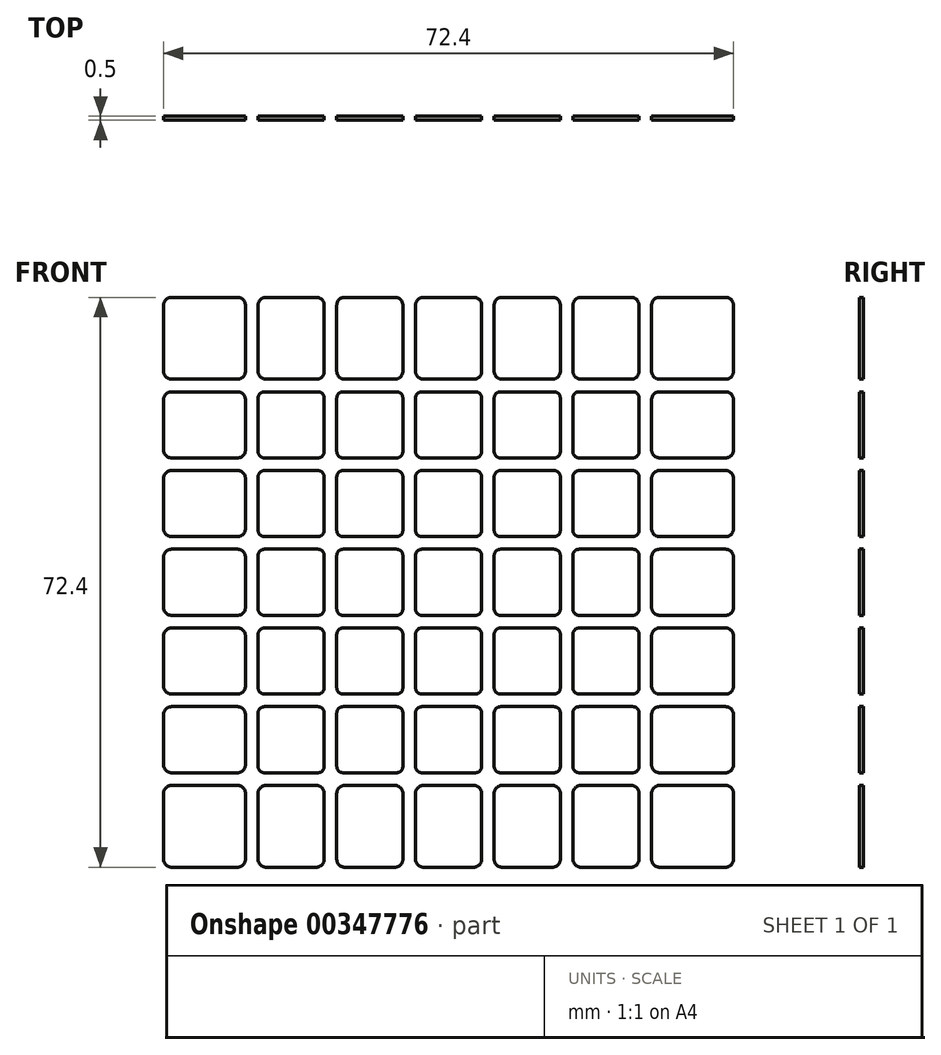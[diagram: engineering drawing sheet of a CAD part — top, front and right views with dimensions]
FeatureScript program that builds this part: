
annotation { "Feature Type Name" : "Feature", "Feature Type Description" : "" }
export const myFeature = defineFeature(function(context is Context, id is Id, definition is map)
    precondition{}
    {
        {
            var Q0;
            Q0=qCreatedBy(makeId("Front.planeOp"),FACE);
            var sketch = newSketch(context, id + "F0", { "sketchPlane" : qUnion([Q0])});
            skLineSegment(sketch, "E0.bottom", {"start": v(3.4, 4.2) * mm, "end": v(-3.4, 4.2) * mm});
            skLineSegment(sketch, "E0.top", {"start": v(3.4, -4.2) * mm, "end": v(-3.4, -4.2) * mm});
            skLineSegment(sketch, "E0.left", {"start": v(4.2, 3.4) * mm, "end": v(4.2, -3.4) * mm});
            skLineSegment(sketch, "E0.right", {"start": v(-4.2, 3.4) * mm, "end": v(-4.2, -3.4) * mm});
            skPoint(sketch, "E0.middle", {"position": v(0, 0) * mm});
            skPoint(sketch, "E1.visualSharp", {"position": v(-4.2, 4.2) * mm});
            skArc(sketch, "E1.filletArc", {"start": v(-3.4, 4.2) * mm, "mid": v(-3.97, 3.97) * mm, "end": v(-4.2, 3.4) * mm});
            skPoint(sketch, "E2.visualSharp", {"position": v(4.2, -4.2) * mm});
            skArc(sketch, "E2.filletArc", {"start": v(3.4, -4.2) * mm, "mid": v(3.97, -3.97) * mm, "end": v(4.2, -3.4) * mm});
            skPoint(sketch, "E3.visualSharp", {"position": v(4.2, 4.2) * mm});
            skArc(sketch, "E3.filletArc", {"start": v(4.2, 3.4) * mm, "mid": v(3.97, 3.97) * mm, "end": v(3.4, 4.2) * mm});
            skPoint(sketch, "E4.visualSharp", {"position": v(-4.2, -4.2) * mm});
            skArc(sketch, "E4.filletArc", {"start": v(-4.2, -3.4) * mm, "mid": v(-3.97, -3.97) * mm, "end": v(-3.4, -4.2) * mm});
            skPoint(sketch, "E5.1.0.0", {"position": v(10, 0) * mm});
            skPoint(sketch, "E5.1.0.1", {"position": v(5.8, 4.2) * mm});
            skPoint(sketch, "E5.1.0.2", {"position": v(14.2, -4.2) * mm});
            skLineSegment(sketch, "E5.1.0.3", {"start": v(5.8, 3.4) * mm, "end": v(5.8, -3.4) * mm});
            skLineSegment(sketch, "E5.1.0.4", {"start": v(14.2, 3.4) * mm, "end": v(14.2, -3.4) * mm});
            skPoint(sketch, "E5.1.0.5", {"position": v(14.2, 4.2) * mm});
            skLineSegment(sketch, "E5.1.0.6", {"start": v(13.4, -4.2) * mm, "end": v(6.6, -4.2) * mm});
            skLineSegment(sketch, "E5.1.0.7", {"start": v(13.4, 4.2) * mm, "end": v(6.6, 4.2) * mm});
            skPoint(sketch, "E5.1.0.8", {"position": v(5.8, -4.2) * mm});
            skArc(sketch, "E5.1.0.9", {"start": v(14.2, 3.4) * mm, "mid": v(13.97, 3.97) * mm, "end": v(13.4, 4.2) * mm});
            skArc(sketch, "E5.1.0.10", {"start": v(13.4, -4.2) * mm, "mid": v(13.97, -3.97) * mm, "end": v(14.2, -3.4) * mm});
            skArc(sketch, "E5.1.0.11", {"start": v(6.6, 4.2) * mm, "mid": v(6.03, 3.97) * mm, "end": v(5.8, 3.4) * mm});
            skArc(sketch, "E5.1.0.12", {"start": v(5.8, -3.4) * mm, "mid": v(6.03, -3.97) * mm, "end": v(6.6, -4.2) * mm});
            skPoint(sketch, "E5.2.0.0", {"position": v(20, 0) * mm});
            skPoint(sketch, "E5.2.0.1", {"position": v(15.8, 4.2) * mm});
            skPoint(sketch, "E5.2.0.2", {"position": v(24.2, -4.2) * mm});
            skLineSegment(sketch, "E5.2.0.3", {"start": v(15.8, 3.4) * mm, "end": v(15.8, -3.4) * mm});
            skLineSegment(sketch, "E5.2.0.4", {"start": v(24.2, 3.4) * mm, "end": v(24.2, -3.4) * mm});
            skPoint(sketch, "E5.2.0.5", {"position": v(24.2, 4.2) * mm});
            skLineSegment(sketch, "E5.2.0.6", {"start": v(23.4, -4.2) * mm, "end": v(16.6, -4.2) * mm});
            skLineSegment(sketch, "E5.2.0.7", {"start": v(23.4, 4.2) * mm, "end": v(16.6, 4.2) * mm});
            skPoint(sketch, "E5.2.0.8", {"position": v(15.8, -4.2) * mm});
            skArc(sketch, "E5.2.0.9", {"start": v(24.2, 3.4) * mm, "mid": v(23.97, 3.97) * mm, "end": v(23.4, 4.2) * mm});
            skArc(sketch, "E5.2.0.10", {"start": v(23.4, -4.2) * mm, "mid": v(23.97, -3.97) * mm, "end": v(24.2, -3.4) * mm});
            skArc(sketch, "E5.2.0.11", {"start": v(16.6, 4.2) * mm, "mid": v(16.03, 3.97) * mm, "end": v(15.8, 3.4) * mm});
            skArc(sketch, "E5.2.0.12", {"start": v(15.8, -3.4) * mm, "mid": v(16.03, -3.97) * mm, "end": v(16.6, -4.2) * mm});
            skLineSegment(sketch, "E5.direction1", {"start": v(-4.2, -4.2) * mm, "end": v(5.8, -4.2) * mm, "construction": true});
            skLineSegment(sketch, "E6.bottom", {"start": v(26.8, -4.2) * mm, "end": v(35.2, -4.2) * mm});
            skLineSegment(sketch, "E6.top", {"start": v(26.8, 4.2) * mm, "end": v(35.2, 4.2) * mm});
            skLineSegment(sketch, "E6.left", {"start": v(25.8, -3.2) * mm, "end": v(25.8, 3.2) * mm});
            skLineSegment(sketch, "E6.right", {"start": v(36.2, -3.2) * mm, "end": v(36.2, 3.2) * mm});
            skPoint(sketch, "E7.visualSharp", {"position": v(25.8, 4.2) * mm});
            skArc(sketch, "E7.filletArc", {"start": v(26.8, 4.2) * mm, "mid": v(26.1, 3.9) * mm, "end": v(25.8, 3.2) * mm});
            skPoint(sketch, "E8.visualSharp", {"position": v(25.8, -4.2) * mm});
            skArc(sketch, "E8.filletArc", {"start": v(25.8, -3.2) * mm, "mid": v(26.1, -3.9) * mm, "end": v(26.8, -4.2) * mm});
            skPoint(sketch, "E9.visualSharp", {"position": v(36.2, 4.2) * mm});
            skArc(sketch, "E9.filletArc", {"start": v(36.2, 3.2) * mm, "mid": v(35.9, 3.9) * mm, "end": v(35.2, 4.2) * mm});
            skPoint(sketch, "E10.visualSharp", {"position": v(36.2, -4.2) * mm});
            skArc(sketch, "E10.filletArc", {"start": v(35.2, -4.2) * mm, "mid": v(35.9, -3.9) * mm, "end": v(36.2, -3.2) * mm});
            skPoint(sketch, "E11.0.1.0", {"position": v(24.2, 14.2) * mm});
            skPoint(sketch, "E11.0.1.1", {"position": v(10, 10) * mm});
            skLineSegment(sketch, "E11.0.1.2", {"start": v(15.8, 13.4) * mm, "end": v(15.8, 6.6) * mm});
            skPoint(sketch, "E11.0.1.3", {"position": v(5.8, 5.8) * mm});
            skPoint(sketch, "E11.0.1.4", {"position": v(25.8, 5.8) * mm});
            skPoint(sketch, "E11.0.1.5", {"position": v(24.2, 5.8) * mm});
            skLineSegment(sketch, "E11.0.1.6", {"start": v(25.8, 6.8) * mm, "end": v(25.8, 13.2) * mm});
            skLineSegment(sketch, "E11.0.1.7", {"start": v(13.4, 14.2) * mm, "end": v(6.6, 14.2) * mm});
            skLineSegment(sketch, "E11.0.1.8", {"start": v(23.4, 14.2) * mm, "end": v(16.6, 14.2) * mm});
            skLineSegment(sketch, "E11.0.1.9", {"start": v(26.8, 14.2) * mm, "end": v(35.2, 14.2) * mm});
            skLineSegment(sketch, "E11.0.1.10", {"start": v(5.8, 13.4) * mm, "end": v(5.8, 6.6) * mm});
            skLineSegment(sketch, "E11.0.1.11", {"start": v(26.8, 5.8) * mm, "end": v(35.2, 5.8) * mm});
            skLineSegment(sketch, "E11.0.1.12", {"start": v(36.2, 6.8) * mm, "end": v(36.2, 13.2) * mm});
            skPoint(sketch, "E11.0.1.13", {"position": v(5.8, 14.2) * mm});
            skPoint(sketch, "E11.0.1.14", {"position": v(25.8, 14.2) * mm});
            skPoint(sketch, "E11.0.1.15", {"position": v(14.2, 5.8) * mm});
            skPoint(sketch, "E11.0.1.16", {"position": v(20, 10) * mm});
            skLineSegment(sketch, "E11.0.1.17", {"start": v(14.2, 13.4) * mm, "end": v(14.2, 6.6) * mm});
            skLineSegment(sketch, "E11.0.1.18", {"start": v(13.4, 5.8) * mm, "end": v(6.6, 5.8) * mm});
            skPoint(sketch, "E11.0.1.19", {"position": v(14.2, 14.2) * mm});
            skPoint(sketch, "E11.0.1.20", {"position": v(15.8, 14.2) * mm});
            skPoint(sketch, "E11.0.1.21", {"position": v(36.2, 14.2) * mm});
            skLineSegment(sketch, "E11.0.1.22", {"start": v(23.4, 5.8) * mm, "end": v(16.6, 5.8) * mm});
            skLineSegment(sketch, "E11.0.1.23", {"start": v(24.2, 13.4) * mm, "end": v(24.2, 6.6) * mm});
            skPoint(sketch, "E11.0.1.24", {"position": v(15.8, 5.8) * mm});
            skPoint(sketch, "E11.0.1.25", {"position": v(36.2, 5.8) * mm});
            skArc(sketch, "E11.0.1.26", {"start": v(35.2, 5.8) * mm, "mid": v(35.9, 6.1) * mm, "end": v(36.2, 6.8) * mm});
            skArc(sketch, "E11.0.1.27", {"start": v(13.4, 5.8) * mm, "mid": v(13.97, 6.03) * mm, "end": v(14.2, 6.6) * mm});
            skArc(sketch, "E11.0.1.28", {"start": v(24.2, 13.4) * mm, "mid": v(23.97, 13.97) * mm, "end": v(23.4, 14.2) * mm});
            skArc(sketch, "E11.0.1.29", {"start": v(15.8, 6.6) * mm, "mid": v(16.03, 6.03) * mm, "end": v(16.6, 5.8) * mm});
            skArc(sketch, "E11.0.1.30", {"start": v(14.2, 13.4) * mm, "mid": v(13.97, 13.97) * mm, "end": v(13.4, 14.2) * mm});
            skArc(sketch, "E11.0.1.31", {"start": v(36.2, 13.2) * mm, "mid": v(35.9, 13.9) * mm, "end": v(35.2, 14.2) * mm});
            skArc(sketch, "E11.0.1.32", {"start": v(23.4, 5.8) * mm, "mid": v(23.97, 6.03) * mm, "end": v(24.2, 6.6) * mm});
            skArc(sketch, "E11.0.1.33", {"start": v(6.6, 14.2) * mm, "mid": v(6.03, 13.97) * mm, "end": v(5.8, 13.4) * mm});
            skArc(sketch, "E11.0.1.34", {"start": v(25.8, 6.8) * mm, "mid": v(26.1, 6.1) * mm, "end": v(26.8, 5.8) * mm});
            skArc(sketch, "E11.0.1.35", {"start": v(16.6, 14.2) * mm, "mid": v(16.03, 13.97) * mm, "end": v(15.8, 13.4) * mm});
            skArc(sketch, "E11.0.1.36", {"start": v(26.8, 14.2) * mm, "mid": v(26.1, 13.9) * mm, "end": v(25.8, 13.2) * mm});
            skArc(sketch, "E11.0.1.37", {"start": v(5.8, 6.6) * mm, "mid": v(6.03, 6.03) * mm, "end": v(6.6, 5.8) * mm});
            skPoint(sketch, "E11.0.2.0", {"position": v(24.2, 24.2) * mm});
            skPoint(sketch, "E11.0.2.1", {"position": v(10, 20) * mm});
            skLineSegment(sketch, "E11.0.2.2", {"start": v(15.8, 23.4) * mm, "end": v(15.8, 16.6) * mm});
            skPoint(sketch, "E11.0.2.3", {"position": v(5.8, 15.8) * mm});
            skPoint(sketch, "E11.0.2.4", {"position": v(25.8, 15.8) * mm});
            skPoint(sketch, "E11.0.2.5", {"position": v(24.2, 15.8) * mm});
            skLineSegment(sketch, "E11.0.2.6", {"start": v(25.8, 16.8) * mm, "end": v(25.8, 23.2) * mm});
            skLineSegment(sketch, "E11.0.2.7", {"start": v(13.4, 24.2) * mm, "end": v(6.6, 24.2) * mm});
            skLineSegment(sketch, "E11.0.2.8", {"start": v(23.4, 24.2) * mm, "end": v(16.6, 24.2) * mm});
            skLineSegment(sketch, "E11.0.2.9", {"start": v(26.8, 24.2) * mm, "end": v(35.2, 24.2) * mm});
            skLineSegment(sketch, "E11.0.2.10", {"start": v(5.8, 23.4) * mm, "end": v(5.8, 16.6) * mm});
            skLineSegment(sketch, "E11.0.2.11", {"start": v(26.8, 15.8) * mm, "end": v(35.2, 15.8) * mm});
            skLineSegment(sketch, "E11.0.2.12", {"start": v(36.2, 16.8) * mm, "end": v(36.2, 23.2) * mm});
            skPoint(sketch, "E11.0.2.13", {"position": v(5.8, 24.2) * mm});
            skPoint(sketch, "E11.0.2.14", {"position": v(25.8, 24.2) * mm});
            skPoint(sketch, "E11.0.2.15", {"position": v(14.2, 15.8) * mm});
            skPoint(sketch, "E11.0.2.16", {"position": v(20, 20) * mm});
            skLineSegment(sketch, "E11.0.2.17", {"start": v(14.2, 23.4) * mm, "end": v(14.2, 16.6) * mm});
            skLineSegment(sketch, "E11.0.2.18", {"start": v(13.4, 15.8) * mm, "end": v(6.6, 15.8) * mm});
            skPoint(sketch, "E11.0.2.19", {"position": v(14.2, 24.2) * mm});
            skPoint(sketch, "E11.0.2.20", {"position": v(15.8, 24.2) * mm});
            skPoint(sketch, "E11.0.2.21", {"position": v(36.2, 24.2) * mm});
            skLineSegment(sketch, "E11.0.2.22", {"start": v(23.4, 15.8) * mm, "end": v(16.6, 15.8) * mm});
            skLineSegment(sketch, "E11.0.2.23", {"start": v(24.2, 23.4) * mm, "end": v(24.2, 16.6) * mm});
            skPoint(sketch, "E11.0.2.24", {"position": v(15.8, 15.8) * mm});
            skPoint(sketch, "E11.0.2.25", {"position": v(36.2, 15.8) * mm});
            skArc(sketch, "E11.0.2.26", {"start": v(35.2, 15.8) * mm, "mid": v(35.9, 16.1) * mm, "end": v(36.2, 16.8) * mm});
            skArc(sketch, "E11.0.2.27", {"start": v(13.4, 15.8) * mm, "mid": v(13.97, 16.03) * mm, "end": v(14.2, 16.6) * mm});
            skArc(sketch, "E11.0.2.28", {"start": v(24.2, 23.4) * mm, "mid": v(23.97, 23.97) * mm, "end": v(23.4, 24.2) * mm});
            skArc(sketch, "E11.0.2.29", {"start": v(15.8, 16.6) * mm, "mid": v(16.03, 16.03) * mm, "end": v(16.6, 15.8) * mm});
            skArc(sketch, "E11.0.2.30", {"start": v(14.2, 23.4) * mm, "mid": v(13.97, 23.97) * mm, "end": v(13.4, 24.2) * mm});
            skArc(sketch, "E11.0.2.31", {"start": v(36.2, 23.2) * mm, "mid": v(35.9, 23.9) * mm, "end": v(35.2, 24.2) * mm});
            skArc(sketch, "E11.0.2.32", {"start": v(23.4, 15.8) * mm, "mid": v(23.97, 16.03) * mm, "end": v(24.2, 16.6) * mm});
            skArc(sketch, "E11.0.2.33", {"start": v(6.6, 24.2) * mm, "mid": v(6.03, 23.97) * mm, "end": v(5.8, 23.4) * mm});
            skArc(sketch, "E11.0.2.34", {"start": v(25.8, 16.8) * mm, "mid": v(26.1, 16.1) * mm, "end": v(26.8, 15.8) * mm});
            skArc(sketch, "E11.0.2.35", {"start": v(16.6, 24.2) * mm, "mid": v(16.03, 23.97) * mm, "end": v(15.8, 23.4) * mm});
            skArc(sketch, "E11.0.2.36", {"start": v(26.8, 24.2) * mm, "mid": v(26.1, 23.9) * mm, "end": v(25.8, 23.2) * mm});
            skArc(sketch, "E11.0.2.37", {"start": v(5.8, 16.6) * mm, "mid": v(6.03, 16.03) * mm, "end": v(6.6, 15.8) * mm});
            skLineSegment(sketch, "E11.direction1", {"start": v(5.8, -4.2) * mm, "end": v(32.07, -4.2) * mm, "construction": true});
            skLineSegment(sketch, "E11.direction2", {"start": v(5.8, -4.2) * mm, "end": v(5.8, 5.8) * mm, "construction": true});
            skLineSegment(sketch, "E12.bottom", {"start": v(26.8, 25.8) * mm, "end": v(35.2, 25.8) * mm});
            skLineSegment(sketch, "E12.top", {"start": v(26.8, 36.2) * mm, "end": v(35.2, 36.2) * mm});
            skLineSegment(sketch, "E12.left", {"start": v(25.8, 26.8) * mm, "end": v(25.8, 35.2) * mm});
            skLineSegment(sketch, "E12.right", {"start": v(36.2, 26.8) * mm, "end": v(36.2, 35.2) * mm});
            skPoint(sketch, "E13.visualSharp", {"position": v(25.8, 25.8) * mm});
            skArc(sketch, "E13.filletArc", {"start": v(25.8, 26.8) * mm, "mid": v(26.1, 26.1) * mm, "end": v(26.8, 25.8) * mm});
            skPoint(sketch, "E14.visualSharp", {"position": v(36.2, 25.8) * mm});
            skArc(sketch, "E14.filletArc", {"start": v(35.2, 25.8) * mm, "mid": v(35.9, 26.1) * mm, "end": v(36.2, 26.8) * mm});
            skPoint(sketch, "E15.visualSharp", {"position": v(36.2, 36.2) * mm});
            skArc(sketch, "E15.filletArc", {"start": v(36.2, 35.2) * mm, "mid": v(35.9, 35.9) * mm, "end": v(35.2, 36.2) * mm});
            skPoint(sketch, "E16.visualSharp", {"position": v(25.8, 36.2) * mm});
            skArc(sketch, "E16.filletArc", {"start": v(26.8, 36.2) * mm, "mid": v(26.1, 35.9) * mm, "end": v(25.8, 35.2) * mm});
            skPoint(sketch, "E17.0.1.0", {"position": v(36.2, -5.8) * mm});
            skPoint(sketch, "E17.0.1.1", {"position": v(36.2, -14.2) * mm});
            skLineSegment(sketch, "E17.0.1.2", {"start": v(36.2, -13.2) * mm, "end": v(36.2, -6.8) * mm});
            skLineSegment(sketch, "E17.0.1.3", {"start": v(25.8, -13.2) * mm, "end": v(25.8, -6.8) * mm});
            skPoint(sketch, "E17.0.1.4", {"position": v(25.8, -5.8) * mm});
            skLineSegment(sketch, "E17.0.1.5", {"start": v(26.8, -14.2) * mm, "end": v(35.2, -14.2) * mm});
            skLineSegment(sketch, "E17.0.1.6", {"start": v(26.8, -5.8) * mm, "end": v(35.2, -5.8) * mm});
            skPoint(sketch, "E17.0.1.7", {"position": v(25.8, -14.2) * mm});
            skArc(sketch, "E17.0.1.8", {"start": v(26.8, -5.8) * mm, "mid": v(26.1, -6.1) * mm, "end": v(25.8, -6.8) * mm});
            skArc(sketch, "E17.0.1.9", {"start": v(25.8, -13.2) * mm, "mid": v(26.1, -13.9) * mm, "end": v(26.8, -14.2) * mm});
            skArc(sketch, "E17.0.1.10", {"start": v(36.2, -6.8) * mm, "mid": v(35.9, -6.1) * mm, "end": v(35.2, -5.8) * mm});
            skArc(sketch, "E17.0.1.11", {"start": v(35.2, -14.2) * mm, "mid": v(35.9, -13.9) * mm, "end": v(36.2, -13.2) * mm});
            skPoint(sketch, "E17.0.2.0", {"position": v(36.2, -15.8) * mm});
            skPoint(sketch, "E17.0.2.1", {"position": v(36.2, -24.2) * mm});
            skLineSegment(sketch, "E17.0.2.2", {"start": v(36.2, -23.2) * mm, "end": v(36.2, -16.8) * mm});
            skLineSegment(sketch, "E17.0.2.3", {"start": v(25.8, -23.2) * mm, "end": v(25.8, -16.8) * mm});
            skPoint(sketch, "E17.0.2.4", {"position": v(25.8, -15.8) * mm});
            skLineSegment(sketch, "E17.0.2.5", {"start": v(26.8, -24.2) * mm, "end": v(35.2, -24.2) * mm});
            skLineSegment(sketch, "E17.0.2.6", {"start": v(26.8, -15.8) * mm, "end": v(35.2, -15.8) * mm});
            skPoint(sketch, "E17.0.2.7", {"position": v(25.8, -24.2) * mm});
            skArc(sketch, "E17.0.2.8", {"start": v(26.8, -15.8) * mm, "mid": v(26.1, -16.1) * mm, "end": v(25.8, -16.8) * mm});
            skArc(sketch, "E17.0.2.9", {"start": v(25.8, -23.2) * mm, "mid": v(26.1, -23.9) * mm, "end": v(26.8, -24.2) * mm});
            skArc(sketch, "E17.0.2.10", {"start": v(36.2, -16.8) * mm, "mid": v(35.9, -16.1) * mm, "end": v(35.2, -15.8) * mm});
            skArc(sketch, "E17.0.2.11", {"start": v(35.2, -24.2) * mm, "mid": v(35.9, -23.9) * mm, "end": v(36.2, -23.2) * mm});
            skLineSegment(sketch, "E17.direction1", {"start": v(25.8, -4.2) * mm, "end": v(50.07, -4.2) * mm, "construction": true});
            skLineSegment(sketch, "E17.direction2", {"start": v(25.8, -4.2) * mm, "end": v(25.8, -14.2) * mm, "construction": true});
            skLineSegment(sketch, "E18.1.0", {"start": v(-4.2, 26.8) * mm, "end": v(-4.2, 35.2) * mm});
            skPoint(sketch, "E18.1.1", {"position": v(14.2, 36.2) * mm});
            skLineSegment(sketch, "E18.1.2", {"start": v(-16.8, 25.8) * mm, "end": v(-23.2, 25.8) * mm});
            skPoint(sketch, "E18.1.3", {"position": v(-20, 20) * mm});
            skPoint(sketch, "E18.1.4", {"position": v(-36.2, 36.2) * mm});
            skLineSegment(sketch, "E18.1.5", {"start": v(4.2, 25.8) * mm, "end": v(14.2, 25.8) * mm, "construction": true});
            skLineSegment(sketch, "E18.1.6", {"start": v(-26.8, 25.8) * mm, "end": v(-35.2, 25.8) * mm});
            skPoint(sketch, "E18.1.7", {"position": v(-15.8, 25.8) * mm});
            skPoint(sketch, "E18.1.8", {"position": v(-4.2, 24.2) * mm});
            skLineSegment(sketch, "E18.1.9", {"start": v(-6.8, 36.2) * mm, "end": v(-13.2, 36.2) * mm});
            skLineSegment(sketch, "E18.1.10", {"start": v(3.2, 36.2) * mm, "end": v(-3.2, 36.2) * mm});
            skPoint(sketch, "E18.1.11", {"position": v(-14.2, 24.2) * mm});
            skLineSegment(sketch, "E18.1.12", {"start": v(24.2, 26.8) * mm, "end": v(24.2, 35.2) * mm});
            skLineSegment(sketch, "E18.1.13", {"start": v(-14.2, 26.8) * mm, "end": v(-14.2, 35.2) * mm});
            skLineSegment(sketch, "E18.1.14", {"start": v(-23.4, 5.8) * mm, "end": v(-16.6, 5.8) * mm});
            skPoint(sketch, "E18.1.15", {"position": v(4.2, 14.2) * mm});
            skPoint(sketch, "E18.1.16", {"position": v(-4.2, 25.8) * mm});
            skPoint(sketch, "E18.1.17", {"position": v(-4.2, 15.8) * mm});
            skPoint(sketch, "E18.1.18", {"position": v(-4.2, 14.2) * mm});
            skPoint(sketch, "E18.1.19", {"position": v(-14.2, 14.2) * mm});
            skLineSegment(sketch, "E18.1.20", {"start": v(-26.8, 36.2) * mm, "end": v(-35.2, 36.2) * mm});
            skLineSegment(sketch, "E18.1.21", {"start": v(-13.4, 5.8) * mm, "end": v(-6.6, 5.8) * mm});
            skLineSegment(sketch, "E18.1.22", {"start": v(15.8, 26.8) * mm, "end": v(15.8, 35.2) * mm});
            skPoint(sketch, "E18.1.23", {"position": v(4.2, 5.8) * mm});
            skLineSegment(sketch, "E18.1.24", {"start": v(5.8, 26.8) * mm, "end": v(5.8, 35.2) * mm});
            skPoint(sketch, "E18.1.25", {"position": v(0, 20) * mm});
            skPoint(sketch, "E18.1.26", {"position": v(-24.2, 24.2) * mm});
            skPoint(sketch, "E18.1.27", {"position": v(-15.8, 5.8) * mm});
            skLineSegment(sketch, "E18.1.28", {"start": v(-15.8, 26.8) * mm, "end": v(-15.8, 35.2) * mm});
            skPoint(sketch, "E18.1.29", {"position": v(-14.2, 15.8) * mm});
            skPoint(sketch, "E18.1.30", {"position": v(-5.8, 15.8) * mm});
            skPoint(sketch, "E18.1.31", {"position": v(-4.2, 36.2) * mm});
            skPoint(sketch, "E18.1.32", {"position": v(4.2, 25.8) * mm});
            skLineSegment(sketch, "E18.1.33", {"start": v(-23.4, 15.8) * mm, "end": v(-16.6, 15.8) * mm});
            skPoint(sketch, "E18.1.34", {"position": v(-24.2, 5.8) * mm});
            skLineSegment(sketch, "E18.1.35", {"start": v(-13.4, 14.2) * mm, "end": v(-6.6, 14.2) * mm});
            skPoint(sketch, "E18.1.36", {"position": v(-36.2, 25.8) * mm});
            skPoint(sketch, "E18.1.37", {"position": v(-5.8, 5.8) * mm});
            skPoint(sketch, "E18.1.38", {"position": v(14.2, 25.8) * mm});
            skLineSegment(sketch, "E18.1.39", {"start": v(-5.8, 26.8) * mm, "end": v(-5.8, 35.2) * mm});
            skLineSegment(sketch, "E18.1.40", {"start": v(-5.8, 13.4) * mm, "end": v(-5.8, 6.6) * mm});
            skLineSegment(sketch, "E18.1.41", {"start": v(-3.4, 14.2) * mm, "end": v(3.4, 14.2) * mm});
            skPoint(sketch, "E18.1.42", {"position": v(5.8, 36.2) * mm});
            skPoint(sketch, "E18.1.43", {"position": v(-5.8, 36.2) * mm});
            skLineSegment(sketch, "E18.1.44", {"start": v(23.2, 25.8) * mm, "end": v(16.8, 25.8) * mm});
            skLineSegment(sketch, "E18.1.45", {"start": v(-14.2, 23.4) * mm, "end": v(-14.2, 16.6) * mm});
            skLineSegment(sketch, "E18.1.46", {"start": v(-23.4, 24.2) * mm, "end": v(-16.6, 24.2) * mm});
            skPoint(sketch, "E18.1.47", {"position": v(-10, 20) * mm});
            skPoint(sketch, "E18.1.48", {"position": v(-20, 10) * mm});
            skPoint(sketch, "E18.1.49", {"position": v(-14.2, 36.2) * mm});
            skLineSegment(sketch, "E18.1.50", {"start": v(-13.4, 24.2) * mm, "end": v(-6.6, 24.2) * mm});
            skLineSegment(sketch, "E18.1.51", {"start": v(-24.2, 23.4) * mm, "end": v(-24.2, 16.6) * mm});
            skPoint(sketch, "E18.1.52", {"position": v(-15.8, 14.2) * mm});
            skLineSegment(sketch, "E18.1.53", {"start": v(-36.2, 26.8) * mm, "end": v(-36.2, 35.2) * mm});
            skPoint(sketch, "E18.1.54", {"position": v(-15.8, 36.2) * mm});
            skPoint(sketch, "E18.1.55", {"position": v(24.2, 25.8) * mm});
            skPoint(sketch, "E18.1.56", {"position": v(-4.2, 5.8) * mm});
            skPoint(sketch, "E18.1.57", {"position": v(-5.8, 14.2) * mm});
            skPoint(sketch, "E18.1.58", {"position": v(4.2, 24.2) * mm});
            skPoint(sketch, "E18.1.59", {"position": v(-10, 10) * mm});
            skLineSegment(sketch, "E18.1.60", {"start": v(23.2, 36.2) * mm, "end": v(16.8, 36.2) * mm});
            skLineSegment(sketch, "E18.1.61", {"start": v(-14.2, 13.4) * mm, "end": v(-14.2, 6.6) * mm});
            skPoint(sketch, "E18.1.62", {"position": v(5.8, 25.8) * mm});
            skLineSegment(sketch, "E18.1.63", {"start": v(-15.8, 23.4) * mm, "end": v(-15.8, 16.6) * mm});
            skPoint(sketch, "E18.1.64", {"position": v(4.2, 36.2) * mm});
            skPoint(sketch, "E18.1.65", {"position": v(-15.8, 24.2) * mm});
            skLineSegment(sketch, "E18.1.66", {"start": v(-25.8, 26.8) * mm, "end": v(-25.8, 35.2) * mm});
            skLineSegment(sketch, "E18.1.67", {"start": v(-4.2, 23.4) * mm, "end": v(-4.2, 16.6) * mm});
            skPoint(sketch, "E18.1.68", {"position": v(-15.8, 15.8) * mm});
            skPoint(sketch, "E18.1.69", {"position": v(-25.8, 36.2) * mm});
            skPoint(sketch, "E18.1.70", {"position": v(15.8, 25.8) * mm});
            skPoint(sketch, "E18.1.71", {"position": v(0, 10) * mm});
            skPoint(sketch, "E18.1.72", {"position": v(-14.2, 25.8) * mm});
            skLineSegment(sketch, "E18.1.73", {"start": v(14.2, 26.8) * mm, "end": v(14.2, 35.2) * mm});
            skPoint(sketch, "E18.1.74", {"position": v(-24.2, 25.8) * mm});
            skLineSegment(sketch, "E18.1.75", {"start": v(-24.2, 13.4) * mm, "end": v(-24.2, 6.6) * mm});
            skLineSegment(sketch, "E18.1.76", {"start": v(-5.8, 23.4) * mm, "end": v(-5.8, 16.6) * mm});
            skLineSegment(sketch, "E18.1.77", {"start": v(3.2, 25.8) * mm, "end": v(-3.2, 25.8) * mm});
            skLineSegment(sketch, "E18.1.78", {"start": v(-4.2, 13.4) * mm, "end": v(-4.2, 6.6) * mm});
            skLineSegment(sketch, "E18.1.79", {"start": v(-24.2, 26.8) * mm, "end": v(-24.2, 35.2) * mm});
            skLineSegment(sketch, "E18.1.80", {"start": v(13.2, 36.2) * mm, "end": v(6.8, 36.2) * mm});
            skPoint(sketch, "E18.1.81", {"position": v(-5.8, 25.8) * mm});
            skPoint(sketch, "E18.1.82", {"position": v(4.2, 15.8) * mm});
            skPoint(sketch, "E18.1.83", {"position": v(-24.2, 14.2) * mm});
            skLineSegment(sketch, "E18.1.84", {"start": v(-3.4, 15.8) * mm, "end": v(3.4, 15.8) * mm});
            skLineSegment(sketch, "E18.1.85", {"start": v(-16.8, 36.2) * mm, "end": v(-23.2, 36.2) * mm});
            skPoint(sketch, "E18.1.86", {"position": v(-5.8, 24.2) * mm});
            skPoint(sketch, "E18.1.87", {"position": v(15.8, 36.2) * mm});
            skPoint(sketch, "E18.1.88", {"position": v(-25.8, 25.8) * mm});
            skPoint(sketch, "E18.1.89", {"position": v(-24.2, 15.8) * mm});
            skLineSegment(sketch, "E18.1.90", {"start": v(-3.4, 24.2) * mm, "end": v(3.4, 24.2) * mm});
            skLineSegment(sketch, "E18.1.91", {"start": v(-23.4, 14.2) * mm, "end": v(-16.6, 14.2) * mm});
            skLineSegment(sketch, "E18.1.92", {"start": v(-13.4, 15.8) * mm, "end": v(-6.6, 15.8) * mm});
            skPoint(sketch, "E18.1.93", {"position": v(-14.2, 5.8) * mm});
            skPoint(sketch, "E18.1.94", {"position": v(24.2, 36.2) * mm});
            skPoint(sketch, "E18.1.95", {"position": v(-24.2, 36.2) * mm});
            skLineSegment(sketch, "E18.1.96", {"start": v(4.2, 5.8) * mm, "end": v(-5.8, 5.8) * mm, "construction": true});
            skLineSegment(sketch, "E18.1.97", {"start": v(-15.8, 13.4) * mm, "end": v(-15.8, 6.6) * mm});
            skLineSegment(sketch, "E18.1.98", {"start": v(-6.8, 25.8) * mm, "end": v(-13.2, 25.8) * mm});
            skLineSegment(sketch, "E18.1.99", {"start": v(-3.4, 5.8) * mm, "end": v(3.4, 5.8) * mm});
            skLineSegment(sketch, "E18.1.100", {"start": v(13.2, 25.8) * mm, "end": v(6.8, 25.8) * mm});
            skLineSegment(sketch, "E18.1.101", {"start": v(4.2, 26.8) * mm, "end": v(4.2, 35.2) * mm});
            skLineSegment(sketch, "E18.1.102", {"start": v(4.2, 13.4) * mm, "end": v(4.2, 6.6) * mm});
            skLineSegment(sketch, "E18.1.103", {"start": v(4.2, 23.4) * mm, "end": v(4.2, 16.6) * mm});
            skArc(sketch, "E18.1.104", {"start": v(-36.2, 26.8) * mm, "mid": v(-35.9, 26.1) * mm, "end": v(-35.2, 25.8) * mm});
            skArc(sketch, "E18.1.105", {"start": v(24.2, 35.2) * mm, "mid": v(23.9, 35.9) * mm, "end": v(23.2, 36.2) * mm});
            skArc(sketch, "E18.1.106", {"start": v(-23.2, 36.2) * mm, "mid": v(-23.9, 35.9) * mm, "end": v(-24.2, 35.2) * mm});
            skArc(sketch, "E18.1.107", {"start": v(4.2, 23.4) * mm, "mid": v(3.97, 23.97) * mm, "end": v(3.4, 24.2) * mm});
            skArc(sketch, "E18.1.108", {"start": v(-5.8, 13.4) * mm, "mid": v(-6.03, 13.97) * mm, "end": v(-6.6, 14.2) * mm});
            skArc(sketch, "E18.1.109", {"start": v(-23.4, 14.2) * mm, "mid": v(-23.97, 13.97) * mm, "end": v(-24.2, 13.4) * mm});
            skArc(sketch, "E18.1.110", {"start": v(-6.6, 5.8) * mm, "mid": v(-6.03, 6.03) * mm, "end": v(-5.8, 6.6) * mm});
            skArc(sketch, "E18.1.111", {"start": v(-15.8, 35.2) * mm, "mid": v(-16.1, 35.9) * mm, "end": v(-16.8, 36.2) * mm});
            skArc(sketch, "E18.1.112", {"start": v(-6.8, 25.8) * mm, "mid": v(-6.1, 26.1) * mm, "end": v(-5.8, 26.8) * mm});
            skArc(sketch, "E18.1.113", {"start": v(-24.2, 16.6) * mm, "mid": v(-23.97, 16.03) * mm, "end": v(-23.4, 15.8) * mm});
            skArc(sketch, "E18.1.114", {"start": v(-24.2, 26.8) * mm, "mid": v(-23.9, 26.1) * mm, "end": v(-23.2, 25.8) * mm});
            skArc(sketch, "E18.1.115", {"start": v(-4.2, 16.6) * mm, "mid": v(-3.97, 16.03) * mm, "end": v(-3.4, 15.8) * mm});
            skArc(sketch, "E18.1.116", {"start": v(-15.8, 13.4) * mm, "mid": v(-16.03, 13.97) * mm, "end": v(-16.6, 14.2) * mm});
            skArc(sketch, "E18.1.117", {"start": v(-14.2, 16.6) * mm, "mid": v(-13.97, 16.03) * mm, "end": v(-13.4, 15.8) * mm});
            skArc(sketch, "E18.1.118", {"start": v(5.8, 26.8) * mm, "mid": v(6.1, 26.1) * mm, "end": v(6.8, 25.8) * mm});
            skArc(sketch, "E18.1.119", {"start": v(4.2, 13.4) * mm, "mid": v(3.97, 13.97) * mm, "end": v(3.4, 14.2) * mm});
            skArc(sketch, "E18.1.120", {"start": v(-25.8, 35.2) * mm, "mid": v(-26.1, 35.9) * mm, "end": v(-26.8, 36.2) * mm});
            skArc(sketch, "E18.1.121", {"start": v(-16.6, 15.8) * mm, "mid": v(-16.03, 16.03) * mm, "end": v(-15.8, 16.6) * mm});
            skArc(sketch, "E18.1.122", {"start": v(-14.2, 26.8) * mm, "mid": v(-13.9, 26.1) * mm, "end": v(-13.2, 25.8) * mm});
            skArc(sketch, "E18.1.123", {"start": v(3.4, 15.8) * mm, "mid": v(3.97, 16.03) * mm, "end": v(4.2, 16.6) * mm});
            skArc(sketch, "E18.1.124", {"start": v(23.2, 25.8) * mm, "mid": v(23.9, 26.1) * mm, "end": v(24.2, 26.8) * mm});
            skArc(sketch, "E18.1.125", {"start": v(15.8, 26.8) * mm, "mid": v(16.1, 26.1) * mm, "end": v(16.8, 25.8) * mm});
            skArc(sketch, "E18.1.126", {"start": v(-26.8, 25.8) * mm, "mid": v(-26.1, 26.1) * mm, "end": v(-25.8, 26.8) * mm});
            skArc(sketch, "E18.1.127", {"start": v(-23.4, 24.2) * mm, "mid": v(-23.97, 23.97) * mm, "end": v(-24.2, 23.4) * mm});
            skArc(sketch, "E18.1.128", {"start": v(-13.4, 24.2) * mm, "mid": v(-13.97, 23.97) * mm, "end": v(-14.2, 23.4) * mm});
            skArc(sketch, "E18.1.129", {"start": v(-3.2, 36.2) * mm, "mid": v(-3.9, 35.9) * mm, "end": v(-4.2, 35.2) * mm});
            skArc(sketch, "E18.1.130", {"start": v(-4.2, 6.6) * mm, "mid": v(-3.97, 6.03) * mm, "end": v(-3.4, 5.8) * mm});
            skArc(sketch, "E18.1.131", {"start": v(16.8, 36.2) * mm, "mid": v(16.1, 35.9) * mm, "end": v(15.8, 35.2) * mm});
            skArc(sketch, "E18.1.132", {"start": v(-35.2, 36.2) * mm, "mid": v(-35.9, 35.9) * mm, "end": v(-36.2, 35.2) * mm});
            skArc(sketch, "E18.1.133", {"start": v(-14.2, 6.6) * mm, "mid": v(-13.97, 6.03) * mm, "end": v(-13.4, 5.8) * mm});
            skArc(sketch, "E18.1.134", {"start": v(-24.2, 6.6) * mm, "mid": v(-23.97, 6.03) * mm, "end": v(-23.4, 5.8) * mm});
            skArc(sketch, "E18.1.135", {"start": v(-3.4, 24.2) * mm, "mid": v(-3.97, 23.97) * mm, "end": v(-4.2, 23.4) * mm});
            skArc(sketch, "E18.1.136", {"start": v(-5.8, 23.4) * mm, "mid": v(-6.03, 23.97) * mm, "end": v(-6.6, 24.2) * mm});
            skArc(sketch, "E18.1.137", {"start": v(-4.2, 26.8) * mm, "mid": v(-3.9, 26.1) * mm, "end": v(-3.2, 25.8) * mm});
            skArc(sketch, "E18.1.138", {"start": v(-5.8, 35.2) * mm, "mid": v(-6.1, 35.9) * mm, "end": v(-6.8, 36.2) * mm});
            skArc(sketch, "E18.1.139", {"start": v(-16.8, 25.8) * mm, "mid": v(-16.1, 26.1) * mm, "end": v(-15.8, 26.8) * mm});
            skArc(sketch, "E18.1.140", {"start": v(-3.4, 14.2) * mm, "mid": v(-3.97, 13.97) * mm, "end": v(-4.2, 13.4) * mm});
            skArc(sketch, "E18.1.141", {"start": v(13.2, 25.8) * mm, "mid": v(13.9, 26.1) * mm, "end": v(14.2, 26.8) * mm});
            skArc(sketch, "E18.1.142", {"start": v(-15.8, 23.4) * mm, "mid": v(-16.03, 23.97) * mm, "end": v(-16.6, 24.2) * mm});
            skArc(sketch, "E18.1.143", {"start": v(-16.6, 5.8) * mm, "mid": v(-16.03, 6.03) * mm, "end": v(-15.8, 6.6) * mm});
            skArc(sketch, "E18.1.144", {"start": v(-6.6, 15.8) * mm, "mid": v(-6.03, 16.03) * mm, "end": v(-5.8, 16.6) * mm});
            skArc(sketch, "E18.1.145", {"start": v(4.2, 35.2) * mm, "mid": v(3.9, 35.9) * mm, "end": v(3.2, 36.2) * mm});
            skArc(sketch, "E18.1.146", {"start": v(-13.4, 14.2) * mm, "mid": v(-13.97, 13.97) * mm, "end": v(-14.2, 13.4) * mm});
            skArc(sketch, "E18.1.147", {"start": v(6.8, 36.2) * mm, "mid": v(6.1, 35.9) * mm, "end": v(5.8, 35.2) * mm});
            skArc(sketch, "E18.1.148", {"start": v(-13.2, 36.2) * mm, "mid": v(-13.9, 35.9) * mm, "end": v(-14.2, 35.2) * mm});
            skArc(sketch, "E18.1.149", {"start": v(14.2, 35.2) * mm, "mid": v(13.9, 35.9) * mm, "end": v(13.2, 36.2) * mm});
            skArc(sketch, "E18.1.150", {"start": v(3.2, 25.8) * mm, "mid": v(3.9, 26.1) * mm, "end": v(4.2, 26.8) * mm});
            skArc(sketch, "E18.1.151", {"start": v(3.4, 5.8) * mm, "mid": v(3.97, 6.03) * mm, "end": v(4.2, 6.6) * mm});
            skLineSegment(sketch, "E18.2.0", {"start": v(-26.8, -4.2) * mm, "end": v(-35.2, -4.2) * mm});
            skPoint(sketch, "E18.2.1", {"position": v(-36.2, 14.2) * mm});
            skLineSegment(sketch, "E18.2.2", {"start": v(-25.8, -16.8) * mm, "end": v(-25.8, -23.2) * mm});
            skPoint(sketch, "E18.2.3", {"position": v(-20, -20) * mm});
            skPoint(sketch, "E18.2.4", {"position": v(-36.2, -36.2) * mm});
            skLineSegment(sketch, "E18.2.5", {"start": v(-25.8, 4.2) * mm, "end": v(-25.8, 14.2) * mm, "construction": true});
            skLineSegment(sketch, "E18.2.6", {"start": v(-25.8, -26.8) * mm, "end": v(-25.8, -35.2) * mm});
            skPoint(sketch, "E18.2.7", {"position": v(-25.8, -15.8) * mm});
            skPoint(sketch, "E18.2.8", {"position": v(-24.2, -4.2) * mm});
            skLineSegment(sketch, "E18.2.9", {"start": v(-36.2, -6.8) * mm, "end": v(-36.2, -13.2) * mm});
            skLineSegment(sketch, "E18.2.10", {"start": v(-36.2, 3.2) * mm, "end": v(-36.2, -3.2) * mm});
            skPoint(sketch, "E18.2.11", {"position": v(-24.2, -14.2) * mm});
            skLineSegment(sketch, "E18.2.12", {"start": v(-26.8, 24.2) * mm, "end": v(-35.2, 24.2) * mm});
            skLineSegment(sketch, "E18.2.13", {"start": v(-26.8, -14.2) * mm, "end": v(-35.2, -14.2) * mm});
            skLineSegment(sketch, "E18.2.14", {"start": v(-5.8, -23.4) * mm, "end": v(-5.8, -16.6) * mm});
            skPoint(sketch, "E18.2.15", {"position": v(-14.2, 4.2) * mm});
            skPoint(sketch, "E18.2.16", {"position": v(-25.8, -4.2) * mm});
            skPoint(sketch, "E18.2.17", {"position": v(-15.8, -4.2) * mm});
            skPoint(sketch, "E18.2.18", {"position": v(-14.2, -4.2) * mm});
            skPoint(sketch, "E18.2.19", {"position": v(-14.2, -14.2) * mm});
            skLineSegment(sketch, "E18.2.20", {"start": v(-36.2, -26.8) * mm, "end": v(-36.2, -35.2) * mm});
            skLineSegment(sketch, "E18.2.21", {"start": v(-5.8, -13.4) * mm, "end": v(-5.8, -6.6) * mm});
            skLineSegment(sketch, "E18.2.22", {"start": v(-26.8, 15.8) * mm, "end": v(-35.2, 15.8) * mm});
            skPoint(sketch, "E18.2.23", {"position": v(-5.8, 4.2) * mm});
            skLineSegment(sketch, "E18.2.24", {"start": v(-26.8, 5.8) * mm, "end": v(-35.2, 5.8) * mm});
            skPoint(sketch, "E18.2.25", {"position": v(-20, 0) * mm});
            skPoint(sketch, "E18.2.26", {"position": v(-24.2, -24.2) * mm});
            skPoint(sketch, "E18.2.27", {"position": v(-5.8, -15.8) * mm});
            skLineSegment(sketch, "E18.2.28", {"start": v(-26.8, -15.8) * mm, "end": v(-35.2, -15.8) * mm});
            skPoint(sketch, "E18.2.29", {"position": v(-15.8, -14.2) * mm});
            skPoint(sketch, "E18.2.30", {"position": v(-15.8, -5.8) * mm});
            skPoint(sketch, "E18.2.31", {"position": v(-36.2, -4.2) * mm});
            skPoint(sketch, "E18.2.32", {"position": v(-25.8, 4.2) * mm});
            skLineSegment(sketch, "E18.2.33", {"start": v(-15.8, -23.4) * mm, "end": v(-15.8, -16.6) * mm});
            skPoint(sketch, "E18.2.34", {"position": v(-5.8, -24.2) * mm});
            skLineSegment(sketch, "E18.2.35", {"start": v(-14.2, -13.4) * mm, "end": v(-14.2, -6.6) * mm});
            skPoint(sketch, "E18.2.36", {"position": v(-25.8, -36.2) * mm});
            skPoint(sketch, "E18.2.37", {"position": v(-5.8, -5.8) * mm});
            skPoint(sketch, "E18.2.38", {"position": v(-25.8, 14.2) * mm});
            skLineSegment(sketch, "E18.2.39", {"start": v(-26.8, -5.8) * mm, "end": v(-35.2, -5.8) * mm});
            skLineSegment(sketch, "E18.2.40", {"start": v(-13.4, -5.8) * mm, "end": v(-6.6, -5.8) * mm});
            skLineSegment(sketch, "E18.2.41", {"start": v(-14.2, -3.4) * mm, "end": v(-14.2, 3.4) * mm});
            skPoint(sketch, "E18.2.42", {"position": v(-36.2, 5.8) * mm});
            skPoint(sketch, "E18.2.43", {"position": v(-36.2, -5.8) * mm});
            skLineSegment(sketch, "E18.2.44", {"start": v(-25.8, 23.2) * mm, "end": v(-25.8, 16.8) * mm});
            skLineSegment(sketch, "E18.2.45", {"start": v(-23.4, -14.2) * mm, "end": v(-16.6, -14.2) * mm});
            skLineSegment(sketch, "E18.2.46", {"start": v(-24.2, -23.4) * mm, "end": v(-24.2, -16.6) * mm});
            skPoint(sketch, "E18.2.47", {"position": v(-20, -10) * mm});
            skPoint(sketch, "E18.2.48", {"position": v(-10, -20) * mm});
            skPoint(sketch, "E18.2.49", {"position": v(-36.2, -14.2) * mm});
            skLineSegment(sketch, "E18.2.50", {"start": v(-24.2, -13.4) * mm, "end": v(-24.2, -6.6) * mm});
            skLineSegment(sketch, "E18.2.51", {"start": v(-23.4, -24.2) * mm, "end": v(-16.6, -24.2) * mm});
            skPoint(sketch, "E18.2.52", {"position": v(-14.2, -15.8) * mm});
            skLineSegment(sketch, "E18.2.53", {"start": v(-26.8, -36.2) * mm, "end": v(-35.2, -36.2) * mm});
            skPoint(sketch, "E18.2.54", {"position": v(-36.2, -15.8) * mm});
            skPoint(sketch, "E18.2.55", {"position": v(-25.8, 24.2) * mm});
            skPoint(sketch, "E18.2.56", {"position": v(-5.8, -4.2) * mm});
            skPoint(sketch, "E18.2.57", {"position": v(-14.2, -5.8) * mm});
            skPoint(sketch, "E18.2.58", {"position": v(-24.2, 4.2) * mm});
            skPoint(sketch, "E18.2.59", {"position": v(-10, -10) * mm});
            skLineSegment(sketch, "E18.2.60", {"start": v(-36.2, 23.2) * mm, "end": v(-36.2, 16.8) * mm});
            skLineSegment(sketch, "E18.2.61", {"start": v(-13.4, -14.2) * mm, "end": v(-6.6, -14.2) * mm});
            skPoint(sketch, "E18.2.62", {"position": v(-25.8, 5.8) * mm});
            skLineSegment(sketch, "E18.2.63", {"start": v(-23.4, -15.8) * mm, "end": v(-16.6, -15.8) * mm});
            skPoint(sketch, "E18.2.64", {"position": v(-36.2, 4.2) * mm});
            skPoint(sketch, "E18.2.65", {"position": v(-24.2, -15.8) * mm});
            skLineSegment(sketch, "E18.2.66", {"start": v(-26.8, -25.8) * mm, "end": v(-35.2, -25.8) * mm});
            skLineSegment(sketch, "E18.2.67", {"start": v(-23.4, -4.2) * mm, "end": v(-16.6, -4.2) * mm});
            skPoint(sketch, "E18.2.68", {"position": v(-15.8, -15.8) * mm});
            skPoint(sketch, "E18.2.69", {"position": v(-36.2, -25.8) * mm});
            skPoint(sketch, "E18.2.70", {"position": v(-25.8, 15.8) * mm});
            skPoint(sketch, "E18.2.71", {"position": v(-10, 0) * mm});
            skPoint(sketch, "E18.2.72", {"position": v(-25.8, -14.2) * mm});
            skLineSegment(sketch, "E18.2.73", {"start": v(-26.8, 14.2) * mm, "end": v(-35.2, 14.2) * mm});
            skPoint(sketch, "E18.2.74", {"position": v(-25.8, -24.2) * mm});
            skLineSegment(sketch, "E18.2.75", {"start": v(-13.4, -24.2) * mm, "end": v(-6.6, -24.2) * mm});
            skLineSegment(sketch, "E18.2.76", {"start": v(-23.4, -5.8) * mm, "end": v(-16.6, -5.8) * mm});
            skLineSegment(sketch, "E18.2.77", {"start": v(-25.8, 3.2) * mm, "end": v(-25.8, -3.2) * mm});
            skLineSegment(sketch, "E18.2.78", {"start": v(-13.4, -4.2) * mm, "end": v(-6.6, -4.2) * mm});
            skLineSegment(sketch, "E18.2.79", {"start": v(-26.8, -24.2) * mm, "end": v(-35.2, -24.2) * mm});
            skLineSegment(sketch, "E18.2.80", {"start": v(-36.2, 13.2) * mm, "end": v(-36.2, 6.8) * mm});
            skPoint(sketch, "E18.2.81", {"position": v(-25.8, -5.8) * mm});
            skPoint(sketch, "E18.2.82", {"position": v(-15.8, 4.2) * mm});
            skPoint(sketch, "E18.2.83", {"position": v(-14.2, -24.2) * mm});
            skLineSegment(sketch, "E18.2.84", {"start": v(-15.8, -3.4) * mm, "end": v(-15.8, 3.4) * mm});
            skLineSegment(sketch, "E18.2.85", {"start": v(-36.2, -16.8) * mm, "end": v(-36.2, -23.2) * mm});
            skPoint(sketch, "E18.2.86", {"position": v(-24.2, -5.8) * mm});
            skPoint(sketch, "E18.2.87", {"position": v(-36.2, 15.8) * mm});
            skPoint(sketch, "E18.2.88", {"position": v(-25.8, -25.8) * mm});
            skPoint(sketch, "E18.2.89", {"position": v(-15.8, -24.2) * mm});
            skLineSegment(sketch, "E18.2.90", {"start": v(-24.2, -3.4) * mm, "end": v(-24.2, 3.4) * mm});
            skLineSegment(sketch, "E18.2.91", {"start": v(-14.2, -23.4) * mm, "end": v(-14.2, -16.6) * mm});
            skLineSegment(sketch, "E18.2.92", {"start": v(-15.8, -13.4) * mm, "end": v(-15.8, -6.6) * mm});
            skPoint(sketch, "E18.2.93", {"position": v(-5.8, -14.2) * mm});
            skPoint(sketch, "E18.2.94", {"position": v(-36.2, 24.2) * mm});
            skPoint(sketch, "E18.2.95", {"position": v(-36.2, -24.2) * mm});
            skLineSegment(sketch, "E18.2.96", {"start": v(-5.8, 4.2) * mm, "end": v(-5.8, -5.8) * mm, "construction": true});
            skLineSegment(sketch, "E18.2.97", {"start": v(-13.4, -15.8) * mm, "end": v(-6.6, -15.8) * mm});
            skLineSegment(sketch, "E18.2.98", {"start": v(-25.8, -6.8) * mm, "end": v(-25.8, -13.2) * mm});
            skLineSegment(sketch, "E18.2.99", {"start": v(-5.8, -3.4) * mm, "end": v(-5.8, 3.4) * mm});
            skLineSegment(sketch, "E18.2.100", {"start": v(-25.8, 13.2) * mm, "end": v(-25.8, 6.8) * mm});
            skLineSegment(sketch, "E18.2.101", {"start": v(-26.8, 4.2) * mm, "end": v(-35.2, 4.2) * mm});
            skLineSegment(sketch, "E18.2.102", {"start": v(-13.4, 4.2) * mm, "end": v(-6.6, 4.2) * mm});
            skLineSegment(sketch, "E18.2.103", {"start": v(-23.4, 4.2) * mm, "end": v(-16.6, 4.2) * mm});
            skArc(sketch, "E18.2.104", {"start": v(-26.8, -36.2) * mm, "mid": v(-26.1, -35.9) * mm, "end": v(-25.8, -35.2) * mm});
            skArc(sketch, "E18.2.105", {"start": v(-35.2, 24.2) * mm, "mid": v(-35.9, 23.9) * mm, "end": v(-36.2, 23.2) * mm});
            skArc(sketch, "E18.2.106", {"start": v(-36.2, -23.2) * mm, "mid": v(-35.9, -23.9) * mm, "end": v(-35.2, -24.2) * mm});
            skArc(sketch, "E18.2.107", {"start": v(-23.4, 4.2) * mm, "mid": v(-23.97, 3.97) * mm, "end": v(-24.2, 3.4) * mm});
            skArc(sketch, "E18.2.108", {"start": v(-13.4, -5.8) * mm, "mid": v(-13.97, -6.03) * mm, "end": v(-14.2, -6.6) * mm});
            skArc(sketch, "E18.2.109", {"start": v(-14.2, -23.4) * mm, "mid": v(-13.97, -23.97) * mm, "end": v(-13.4, -24.2) * mm});
            skArc(sketch, "E18.2.110", {"start": v(-5.8, -6.6) * mm, "mid": v(-6.03, -6.03) * mm, "end": v(-6.6, -5.8) * mm});
            skArc(sketch, "E18.2.111", {"start": v(-35.2, -15.8) * mm, "mid": v(-35.9, -16.1) * mm, "end": v(-36.2, -16.8) * mm});
            skArc(sketch, "E18.2.112", {"start": v(-25.8, -6.8) * mm, "mid": v(-26.1, -6.1) * mm, "end": v(-26.8, -5.8) * mm});
            skArc(sketch, "E18.2.113", {"start": v(-16.6, -24.2) * mm, "mid": v(-16.03, -23.97) * mm, "end": v(-15.8, -23.4) * mm});
            skArc(sketch, "E18.2.114", {"start": v(-26.8, -24.2) * mm, "mid": v(-26.1, -23.9) * mm, "end": v(-25.8, -23.2) * mm});
            skArc(sketch, "E18.2.115", {"start": v(-16.6, -4.2) * mm, "mid": v(-16.03, -3.97) * mm, "end": v(-15.8, -3.4) * mm});
            skArc(sketch, "E18.2.116", {"start": v(-13.4, -15.8) * mm, "mid": v(-13.97, -16.03) * mm, "end": v(-14.2, -16.6) * mm});
            skArc(sketch, "E18.2.117", {"start": v(-16.6, -14.2) * mm, "mid": v(-16.03, -13.97) * mm, "end": v(-15.8, -13.4) * mm});
            skArc(sketch, "E18.2.118", {"start": v(-26.8, 5.8) * mm, "mid": v(-26.1, 6.1) * mm, "end": v(-25.8, 6.8) * mm});
            skArc(sketch, "E18.2.119", {"start": v(-13.4, 4.2) * mm, "mid": v(-13.97, 3.97) * mm, "end": v(-14.2, 3.4) * mm});
            skArc(sketch, "E18.2.120", {"start": v(-35.2, -25.8) * mm, "mid": v(-35.9, -26.1) * mm, "end": v(-36.2, -26.8) * mm});
            skArc(sketch, "E18.2.121", {"start": v(-15.8, -16.6) * mm, "mid": v(-16.03, -16.03) * mm, "end": v(-16.6, -15.8) * mm});
            skArc(sketch, "E18.2.122", {"start": v(-26.8, -14.2) * mm, "mid": v(-26.1, -13.9) * mm, "end": v(-25.8, -13.2) * mm});
            skArc(sketch, "E18.2.123", {"start": v(-15.8, 3.4) * mm, "mid": v(-16.03, 3.97) * mm, "end": v(-16.6, 4.2) * mm});
            skArc(sketch, "E18.2.124", {"start": v(-25.8, 23.2) * mm, "mid": v(-26.1, 23.9) * mm, "end": v(-26.8, 24.2) * mm});
            skArc(sketch, "E18.2.125", {"start": v(-26.8, 15.8) * mm, "mid": v(-26.1, 16.1) * mm, "end": v(-25.8, 16.8) * mm});
            skArc(sketch, "E18.2.126", {"start": v(-25.8, -26.8) * mm, "mid": v(-26.1, -26.1) * mm, "end": v(-26.8, -25.8) * mm});
            skArc(sketch, "E18.2.127", {"start": v(-24.2, -23.4) * mm, "mid": v(-23.97, -23.97) * mm, "end": v(-23.4, -24.2) * mm});
            skArc(sketch, "E18.2.128", {"start": v(-24.2, -13.4) * mm, "mid": v(-23.97, -13.97) * mm, "end": v(-23.4, -14.2) * mm});
            skArc(sketch, "E18.2.129", {"start": v(-36.2, -3.2) * mm, "mid": v(-35.9, -3.9) * mm, "end": v(-35.2, -4.2) * mm});
            skArc(sketch, "E18.2.130", {"start": v(-6.6, -4.2) * mm, "mid": v(-6.03, -3.97) * mm, "end": v(-5.8, -3.4) * mm});
            skArc(sketch, "E18.2.131", {"start": v(-36.2, 16.8) * mm, "mid": v(-35.9, 16.1) * mm, "end": v(-35.2, 15.8) * mm});
            skArc(sketch, "E18.2.132", {"start": v(-36.2, -35.2) * mm, "mid": v(-35.9, -35.9) * mm, "end": v(-35.2, -36.2) * mm});
            skArc(sketch, "E18.2.133", {"start": v(-6.6, -14.2) * mm, "mid": v(-6.03, -13.97) * mm, "end": v(-5.8, -13.4) * mm});
            skArc(sketch, "E18.2.134", {"start": v(-6.6, -24.2) * mm, "mid": v(-6.03, -23.97) * mm, "end": v(-5.8, -23.4) * mm});
            skArc(sketch, "E18.2.135", {"start": v(-24.2, -3.4) * mm, "mid": v(-23.97, -3.97) * mm, "end": v(-23.4, -4.2) * mm});
            skArc(sketch, "E18.2.136", {"start": v(-23.4, -5.8) * mm, "mid": v(-23.97, -6.03) * mm, "end": v(-24.2, -6.6) * mm});
            skArc(sketch, "E18.2.137", {"start": v(-26.8, -4.2) * mm, "mid": v(-26.1, -3.9) * mm, "end": v(-25.8, -3.2) * mm});
            skArc(sketch, "E18.2.138", {"start": v(-35.2, -5.8) * mm, "mid": v(-35.9, -6.1) * mm, "end": v(-36.2, -6.8) * mm});
            skArc(sketch, "E18.2.139", {"start": v(-25.8, -16.8) * mm, "mid": v(-26.1, -16.1) * mm, "end": v(-26.8, -15.8) * mm});
            skArc(sketch, "E18.2.140", {"start": v(-14.2, -3.4) * mm, "mid": v(-13.97, -3.97) * mm, "end": v(-13.4, -4.2) * mm});
            skArc(sketch, "E18.2.141", {"start": v(-25.8, 13.2) * mm, "mid": v(-26.1, 13.9) * mm, "end": v(-26.8, 14.2) * mm});
            skArc(sketch, "E18.2.142", {"start": v(-23.4, -15.8) * mm, "mid": v(-23.97, -16.03) * mm, "end": v(-24.2, -16.6) * mm});
            skArc(sketch, "E18.2.143", {"start": v(-5.8, -16.6) * mm, "mid": v(-6.03, -16.03) * mm, "end": v(-6.6, -15.8) * mm});
            skArc(sketch, "E18.2.144", {"start": v(-15.8, -6.6) * mm, "mid": v(-16.03, -6.03) * mm, "end": v(-16.6, -5.8) * mm});
            skArc(sketch, "E18.2.145", {"start": v(-35.2, 4.2) * mm, "mid": v(-35.9, 3.9) * mm, "end": v(-36.2, 3.2) * mm});
            skArc(sketch, "E18.2.146", {"start": v(-14.2, -13.4) * mm, "mid": v(-13.97, -13.97) * mm, "end": v(-13.4, -14.2) * mm});
            skArc(sketch, "E18.2.147", {"start": v(-36.2, 6.8) * mm, "mid": v(-35.9, 6.1) * mm, "end": v(-35.2, 5.8) * mm});
            skArc(sketch, "E18.2.148", {"start": v(-36.2, -13.2) * mm, "mid": v(-35.9, -13.9) * mm, "end": v(-35.2, -14.2) * mm});
            skArc(sketch, "E18.2.149", {"start": v(-35.2, 14.2) * mm, "mid": v(-35.9, 13.9) * mm, "end": v(-36.2, 13.2) * mm});
            skArc(sketch, "E18.2.150", {"start": v(-25.8, 3.2) * mm, "mid": v(-26.1, 3.9) * mm, "end": v(-26.8, 4.2) * mm});
            skArc(sketch, "E18.2.151", {"start": v(-5.8, 3.4) * mm, "mid": v(-6.03, 3.97) * mm, "end": v(-6.6, 4.2) * mm});
            skLineSegment(sketch, "E18.3.0", {"start": v(4.2, -26.8) * mm, "end": v(4.2, -35.2) * mm});
            skPoint(sketch, "E18.3.1", {"position": v(-14.2, -36.2) * mm});
            skLineSegment(sketch, "E18.3.2", {"start": v(16.8, -25.8) * mm, "end": v(23.2, -25.8) * mm});
            skPoint(sketch, "E18.3.3", {"position": v(20, -20) * mm});
            skPoint(sketch, "E18.3.4", {"position": v(36.2, -36.2) * mm});
            skLineSegment(sketch, "E18.3.5", {"start": v(-4.2, -25.8) * mm, "end": v(-14.2, -25.8) * mm, "construction": true});
            skLineSegment(sketch, "E18.3.6", {"start": v(26.8, -25.8) * mm, "end": v(35.2, -25.8) * mm});
            skPoint(sketch, "E18.3.7", {"position": v(15.8, -25.8) * mm});
            skPoint(sketch, "E18.3.8", {"position": v(4.2, -24.2) * mm});
            skLineSegment(sketch, "E18.3.9", {"start": v(6.8, -36.2) * mm, "end": v(13.2, -36.2) * mm});
            skLineSegment(sketch, "E18.3.10", {"start": v(-3.2, -36.2) * mm, "end": v(3.2, -36.2) * mm});
            skPoint(sketch, "E18.3.11", {"position": v(14.2, -24.2) * mm});
            skLineSegment(sketch, "E18.3.12", {"start": v(-24.2, -26.8) * mm, "end": v(-24.2, -35.2) * mm});
            skLineSegment(sketch, "E18.3.13", {"start": v(14.2, -26.8) * mm, "end": v(14.2, -35.2) * mm});
            skLineSegment(sketch, "E18.3.14", {"start": v(23.4, -5.8) * mm, "end": v(16.6, -5.8) * mm});
            skPoint(sketch, "E18.3.15", {"position": v(-4.2, -14.2) * mm});
            skPoint(sketch, "E18.3.16", {"position": v(4.2, -25.8) * mm});
            skPoint(sketch, "E18.3.17", {"position": v(4.2, -15.8) * mm});
            skPoint(sketch, "E18.3.18", {"position": v(4.2, -14.2) * mm});
            skPoint(sketch, "E18.3.19", {"position": v(14.2, -14.2) * mm});
            skLineSegment(sketch, "E18.3.20", {"start": v(26.8, -36.2) * mm, "end": v(35.2, -36.2) * mm});
            skLineSegment(sketch, "E18.3.21", {"start": v(13.4, -5.8) * mm, "end": v(6.6, -5.8) * mm});
            skLineSegment(sketch, "E18.3.22", {"start": v(-15.8, -26.8) * mm, "end": v(-15.8, -35.2) * mm});
            skPoint(sketch, "E18.3.23", {"position": v(-4.2, -5.8) * mm});
            skLineSegment(sketch, "E18.3.24", {"start": v(-5.8, -26.8) * mm, "end": v(-5.8, -35.2) * mm});
            skPoint(sketch, "E18.3.25", {"position": v(0, -20) * mm});
            skPoint(sketch, "E18.3.26", {"position": v(24.2, -24.2) * mm});
            skPoint(sketch, "E18.3.27", {"position": v(15.8, -5.8) * mm});
            skLineSegment(sketch, "E18.3.28", {"start": v(15.8, -26.8) * mm, "end": v(15.8, -35.2) * mm});
            skPoint(sketch, "E18.3.29", {"position": v(14.2, -15.8) * mm});
            skPoint(sketch, "E18.3.30", {"position": v(5.8, -15.8) * mm});
            skPoint(sketch, "E18.3.31", {"position": v(4.2, -36.2) * mm});
            skPoint(sketch, "E18.3.32", {"position": v(-4.2, -25.8) * mm});
            skLineSegment(sketch, "E18.3.33", {"start": v(23.4, -15.8) * mm, "end": v(16.6, -15.8) * mm});
            skPoint(sketch, "E18.3.34", {"position": v(24.2, -5.8) * mm});
            skLineSegment(sketch, "E18.3.35", {"start": v(13.4, -14.2) * mm, "end": v(6.6, -14.2) * mm});
            skPoint(sketch, "E18.3.36", {"position": v(36.2, -25.8) * mm});
            skPoint(sketch, "E18.3.37", {"position": v(5.8, -5.8) * mm});
            skPoint(sketch, "E18.3.38", {"position": v(-14.2, -25.8) * mm});
            skLineSegment(sketch, "E18.3.39", {"start": v(5.8, -26.8) * mm, "end": v(5.8, -35.2) * mm});
            skLineSegment(sketch, "E18.3.40", {"start": v(5.8, -13.4) * mm, "end": v(5.8, -6.6) * mm});
            skLineSegment(sketch, "E18.3.41", {"start": v(3.4, -14.2) * mm, "end": v(-3.4, -14.2) * mm});
            skPoint(sketch, "E18.3.42", {"position": v(-5.8, -36.2) * mm});
            skPoint(sketch, "E18.3.43", {"position": v(5.8, -36.2) * mm});
            skLineSegment(sketch, "E18.3.44", {"start": v(-23.2, -25.8) * mm, "end": v(-16.8, -25.8) * mm});
            skLineSegment(sketch, "E18.3.45", {"start": v(14.2, -23.4) * mm, "end": v(14.2, -16.6) * mm});
            skLineSegment(sketch, "E18.3.46", {"start": v(23.4, -24.2) * mm, "end": v(16.6, -24.2) * mm});
            skPoint(sketch, "E18.3.47", {"position": v(10, -20) * mm});
            skPoint(sketch, "E18.3.48", {"position": v(20, -10) * mm});
            skPoint(sketch, "E18.3.49", {"position": v(14.2, -36.2) * mm});
            skLineSegment(sketch, "E18.3.50", {"start": v(13.4, -24.2) * mm, "end": v(6.6, -24.2) * mm});
            skLineSegment(sketch, "E18.3.51", {"start": v(24.2, -23.4) * mm, "end": v(24.2, -16.6) * mm});
            skPoint(sketch, "E18.3.52", {"position": v(15.8, -14.2) * mm});
            skLineSegment(sketch, "E18.3.53", {"start": v(36.2, -26.8) * mm, "end": v(36.2, -35.2) * mm});
            skPoint(sketch, "E18.3.54", {"position": v(15.8, -36.2) * mm});
            skPoint(sketch, "E18.3.55", {"position": v(-24.2, -25.8) * mm});
            skPoint(sketch, "E18.3.56", {"position": v(4.2, -5.8) * mm});
            skPoint(sketch, "E18.3.57", {"position": v(5.8, -14.2) * mm});
            skPoint(sketch, "E18.3.58", {"position": v(-4.2, -24.2) * mm});
            skPoint(sketch, "E18.3.59", {"position": v(10, -10) * mm});
            skLineSegment(sketch, "E18.3.60", {"start": v(-23.2, -36.2) * mm, "end": v(-16.8, -36.2) * mm});
            skLineSegment(sketch, "E18.3.61", {"start": v(14.2, -13.4) * mm, "end": v(14.2, -6.6) * mm});
            skPoint(sketch, "E18.3.62", {"position": v(-5.8, -25.8) * mm});
            skLineSegment(sketch, "E18.3.63", {"start": v(15.8, -23.4) * mm, "end": v(15.8, -16.6) * mm});
            skPoint(sketch, "E18.3.64", {"position": v(-4.2, -36.2) * mm});
            skPoint(sketch, "E18.3.65", {"position": v(15.8, -24.2) * mm});
            skLineSegment(sketch, "E18.3.66", {"start": v(25.8, -26.8) * mm, "end": v(25.8, -35.2) * mm});
            skLineSegment(sketch, "E18.3.67", {"start": v(4.2, -23.4) * mm, "end": v(4.2, -16.6) * mm});
            skPoint(sketch, "E18.3.68", {"position": v(15.8, -15.8) * mm});
            skPoint(sketch, "E18.3.69", {"position": v(25.8, -36.2) * mm});
            skPoint(sketch, "E18.3.70", {"position": v(-15.8, -25.8) * mm});
            skPoint(sketch, "E18.3.71", {"position": v(0, -10) * mm});
            skPoint(sketch, "E18.3.72", {"position": v(14.2, -25.8) * mm});
            skLineSegment(sketch, "E18.3.73", {"start": v(-14.2, -26.8) * mm, "end": v(-14.2, -35.2) * mm});
            skPoint(sketch, "E18.3.74", {"position": v(24.2, -25.8) * mm});
            skLineSegment(sketch, "E18.3.75", {"start": v(24.2, -13.4) * mm, "end": v(24.2, -6.6) * mm});
            skLineSegment(sketch, "E18.3.76", {"start": v(5.8, -23.4) * mm, "end": v(5.8, -16.6) * mm});
            skLineSegment(sketch, "E18.3.77", {"start": v(-3.2, -25.8) * mm, "end": v(3.2, -25.8) * mm});
            skLineSegment(sketch, "E18.3.78", {"start": v(4.2, -13.4) * mm, "end": v(4.2, -6.6) * mm});
            skLineSegment(sketch, "E18.3.79", {"start": v(24.2, -26.8) * mm, "end": v(24.2, -35.2) * mm});
            skLineSegment(sketch, "E18.3.80", {"start": v(-13.2, -36.2) * mm, "end": v(-6.8, -36.2) * mm});
            skPoint(sketch, "E18.3.81", {"position": v(5.8, -25.8) * mm});
            skPoint(sketch, "E18.3.82", {"position": v(-4.2, -15.8) * mm});
            skPoint(sketch, "E18.3.83", {"position": v(24.2, -14.2) * mm});
            skLineSegment(sketch, "E18.3.84", {"start": v(3.4, -15.8) * mm, "end": v(-3.4, -15.8) * mm});
            skLineSegment(sketch, "E18.3.85", {"start": v(16.8, -36.2) * mm, "end": v(23.2, -36.2) * mm});
            skPoint(sketch, "E18.3.86", {"position": v(5.8, -24.2) * mm});
            skPoint(sketch, "E18.3.87", {"position": v(-15.8, -36.2) * mm});
            skPoint(sketch, "E18.3.88", {"position": v(25.8, -25.8) * mm});
            skPoint(sketch, "E18.3.89", {"position": v(24.2, -15.8) * mm});
            skLineSegment(sketch, "E18.3.90", {"start": v(3.4, -24.2) * mm, "end": v(-3.4, -24.2) * mm});
            skLineSegment(sketch, "E18.3.91", {"start": v(23.4, -14.2) * mm, "end": v(16.6, -14.2) * mm});
            skLineSegment(sketch, "E18.3.92", {"start": v(13.4, -15.8) * mm, "end": v(6.6, -15.8) * mm});
            skPoint(sketch, "E18.3.93", {"position": v(14.2, -5.8) * mm});
            skPoint(sketch, "E18.3.94", {"position": v(-24.2, -36.2) * mm});
            skPoint(sketch, "E18.3.95", {"position": v(24.2, -36.2) * mm});
            skLineSegment(sketch, "E18.3.96", {"start": v(-4.2, -5.8) * mm, "end": v(5.8, -5.8) * mm, "construction": true});
            skLineSegment(sketch, "E18.3.97", {"start": v(15.8, -13.4) * mm, "end": v(15.8, -6.6) * mm});
            skLineSegment(sketch, "E18.3.98", {"start": v(6.8, -25.8) * mm, "end": v(13.2, -25.8) * mm});
            skLineSegment(sketch, "E18.3.99", {"start": v(3.4, -5.8) * mm, "end": v(-3.4, -5.8) * mm});
            skLineSegment(sketch, "E18.3.100", {"start": v(-13.2, -25.8) * mm, "end": v(-6.8, -25.8) * mm});
            skLineSegment(sketch, "E18.3.101", {"start": v(-4.2, -26.8) * mm, "end": v(-4.2, -35.2) * mm});
            skLineSegment(sketch, "E18.3.102", {"start": v(-4.2, -13.4) * mm, "end": v(-4.2, -6.6) * mm});
            skLineSegment(sketch, "E18.3.103", {"start": v(-4.2, -23.4) * mm, "end": v(-4.2, -16.6) * mm});
            skArc(sketch, "E18.3.104", {"start": v(36.2, -26.8) * mm, "mid": v(35.9, -26.1) * mm, "end": v(35.2, -25.8) * mm});
            skArc(sketch, "E18.3.105", {"start": v(-24.2, -35.2) * mm, "mid": v(-23.9, -35.9) * mm, "end": v(-23.2, -36.2) * mm});
            skArc(sketch, "E18.3.106", {"start": v(23.2, -36.2) * mm, "mid": v(23.9, -35.9) * mm, "end": v(24.2, -35.2) * mm});
            skArc(sketch, "E18.3.107", {"start": v(-4.2, -23.4) * mm, "mid": v(-3.97, -23.97) * mm, "end": v(-3.4, -24.2) * mm});
            skArc(sketch, "E18.3.108", {"start": v(5.8, -13.4) * mm, "mid": v(6.03, -13.97) * mm, "end": v(6.6, -14.2) * mm});
            skArc(sketch, "E18.3.109", {"start": v(23.4, -14.2) * mm, "mid": v(23.97, -13.97) * mm, "end": v(24.2, -13.4) * mm});
            skArc(sketch, "E18.3.110", {"start": v(6.6, -5.8) * mm, "mid": v(6.03, -6.03) * mm, "end": v(5.8, -6.6) * mm});
            skArc(sketch, "E18.3.111", {"start": v(15.8, -35.2) * mm, "mid": v(16.1, -35.9) * mm, "end": v(16.8, -36.2) * mm});
            skArc(sketch, "E18.3.112", {"start": v(6.8, -25.8) * mm, "mid": v(6.1, -26.1) * mm, "end": v(5.8, -26.8) * mm});
            skArc(sketch, "E18.3.113", {"start": v(24.2, -16.6) * mm, "mid": v(23.97, -16.03) * mm, "end": v(23.4, -15.8) * mm});
            skArc(sketch, "E18.3.114", {"start": v(24.2, -26.8) * mm, "mid": v(23.9, -26.1) * mm, "end": v(23.2, -25.8) * mm});
            skArc(sketch, "E18.3.115", {"start": v(4.2, -16.6) * mm, "mid": v(3.97, -16.03) * mm, "end": v(3.4, -15.8) * mm});
            skArc(sketch, "E18.3.116", {"start": v(15.8, -13.4) * mm, "mid": v(16.03, -13.97) * mm, "end": v(16.6, -14.2) * mm});
            skArc(sketch, "E18.3.117", {"start": v(14.2, -16.6) * mm, "mid": v(13.97, -16.03) * mm, "end": v(13.4, -15.8) * mm});
            skArc(sketch, "E18.3.118", {"start": v(-5.8, -26.8) * mm, "mid": v(-6.1, -26.1) * mm, "end": v(-6.8, -25.8) * mm});
            skArc(sketch, "E18.3.119", {"start": v(-4.2, -13.4) * mm, "mid": v(-3.97, -13.97) * mm, "end": v(-3.4, -14.2) * mm});
            skArc(sketch, "E18.3.120", {"start": v(25.8, -35.2) * mm, "mid": v(26.1, -35.9) * mm, "end": v(26.8, -36.2) * mm});
            skArc(sketch, "E18.3.121", {"start": v(16.6, -15.8) * mm, "mid": v(16.03, -16.03) * mm, "end": v(15.8, -16.6) * mm});
            skArc(sketch, "E18.3.122", {"start": v(14.2, -26.8) * mm, "mid": v(13.9, -26.1) * mm, "end": v(13.2, -25.8) * mm});
            skArc(sketch, "E18.3.123", {"start": v(-3.4, -15.8) * mm, "mid": v(-3.97, -16.03) * mm, "end": v(-4.2, -16.6) * mm});
            skArc(sketch, "E18.3.124", {"start": v(-23.2, -25.8) * mm, "mid": v(-23.9, -26.1) * mm, "end": v(-24.2, -26.8) * mm});
            skArc(sketch, "E18.3.125", {"start": v(-15.8, -26.8) * mm, "mid": v(-16.1, -26.1) * mm, "end": v(-16.8, -25.8) * mm});
            skArc(sketch, "E18.3.126", {"start": v(26.8, -25.8) * mm, "mid": v(26.1, -26.1) * mm, "end": v(25.8, -26.8) * mm});
            skArc(sketch, "E18.3.127", {"start": v(23.4, -24.2) * mm, "mid": v(23.97, -23.97) * mm, "end": v(24.2, -23.4) * mm});
            skArc(sketch, "E18.3.128", {"start": v(13.4, -24.2) * mm, "mid": v(13.97, -23.97) * mm, "end": v(14.2, -23.4) * mm});
            skArc(sketch, "E18.3.129", {"start": v(3.2, -36.2) * mm, "mid": v(3.9, -35.9) * mm, "end": v(4.2, -35.2) * mm});
            skArc(sketch, "E18.3.130", {"start": v(4.2, -6.6) * mm, "mid": v(3.97, -6.03) * mm, "end": v(3.4, -5.8) * mm});
            skArc(sketch, "E18.3.131", {"start": v(-16.8, -36.2) * mm, "mid": v(-16.1, -35.9) * mm, "end": v(-15.8, -35.2) * mm});
            skArc(sketch, "E18.3.132", {"start": v(35.2, -36.2) * mm, "mid": v(35.9, -35.9) * mm, "end": v(36.2, -35.2) * mm});
            skArc(sketch, "E18.3.133", {"start": v(14.2, -6.6) * mm, "mid": v(13.97, -6.03) * mm, "end": v(13.4, -5.8) * mm});
            skArc(sketch, "E18.3.134", {"start": v(24.2, -6.6) * mm, "mid": v(23.97, -6.03) * mm, "end": v(23.4, -5.8) * mm});
            skArc(sketch, "E18.3.135", {"start": v(3.4, -24.2) * mm, "mid": v(3.97, -23.97) * mm, "end": v(4.2, -23.4) * mm});
            skArc(sketch, "E18.3.136", {"start": v(5.8, -23.4) * mm, "mid": v(6.03, -23.97) * mm, "end": v(6.6, -24.2) * mm});
            skArc(sketch, "E18.3.137", {"start": v(4.2, -26.8) * mm, "mid": v(3.9, -26.1) * mm, "end": v(3.2, -25.8) * mm});
            skArc(sketch, "E18.3.138", {"start": v(5.8, -35.2) * mm, "mid": v(6.1, -35.9) * mm, "end": v(6.8, -36.2) * mm});
            skArc(sketch, "E18.3.139", {"start": v(16.8, -25.8) * mm, "mid": v(16.1, -26.1) * mm, "end": v(15.8, -26.8) * mm});
            skArc(sketch, "E18.3.140", {"start": v(3.4, -14.2) * mm, "mid": v(3.97, -13.97) * mm, "end": v(4.2, -13.4) * mm});
            skArc(sketch, "E18.3.141", {"start": v(-13.2, -25.8) * mm, "mid": v(-13.9, -26.1) * mm, "end": v(-14.2, -26.8) * mm});
            skArc(sketch, "E18.3.142", {"start": v(15.8, -23.4) * mm, "mid": v(16.03, -23.97) * mm, "end": v(16.6, -24.2) * mm});
            skArc(sketch, "E18.3.143", {"start": v(16.6, -5.8) * mm, "mid": v(16.03, -6.03) * mm, "end": v(15.8, -6.6) * mm});
            skArc(sketch, "E18.3.144", {"start": v(6.6, -15.8) * mm, "mid": v(6.03, -16.03) * mm, "end": v(5.8, -16.6) * mm});
            skArc(sketch, "E18.3.145", {"start": v(-4.2, -35.2) * mm, "mid": v(-3.9, -35.9) * mm, "end": v(-3.2, -36.2) * mm});
            skArc(sketch, "E18.3.146", {"start": v(13.4, -14.2) * mm, "mid": v(13.97, -13.97) * mm, "end": v(14.2, -13.4) * mm});
            skArc(sketch, "E18.3.147", {"start": v(-6.8, -36.2) * mm, "mid": v(-6.1, -35.9) * mm, "end": v(-5.8, -35.2) * mm});
            skArc(sketch, "E18.3.148", {"start": v(13.2, -36.2) * mm, "mid": v(13.9, -35.9) * mm, "end": v(14.2, -35.2) * mm});
            skArc(sketch, "E18.3.149", {"start": v(-14.2, -35.2) * mm, "mid": v(-13.9, -35.9) * mm, "end": v(-13.2, -36.2) * mm});
            skArc(sketch, "E18.3.150", {"start": v(-3.2, -25.8) * mm, "mid": v(-3.9, -26.1) * mm, "end": v(-4.2, -26.8) * mm});
            skArc(sketch, "E18.3.151", {"start": v(-3.4, -5.8) * mm, "mid": v(-3.97, -6.03) * mm, "end": v(-4.2, -6.6) * mm});
            skSolve(sketch);
        }
        {
            var Q0;
            Q0 = qSketchRegion(id + "F0", true);
            extrude(context, id + "F1", {"entities" : qUnion([Q0]), "depth" : 0.5 * mm});
        }
    });
